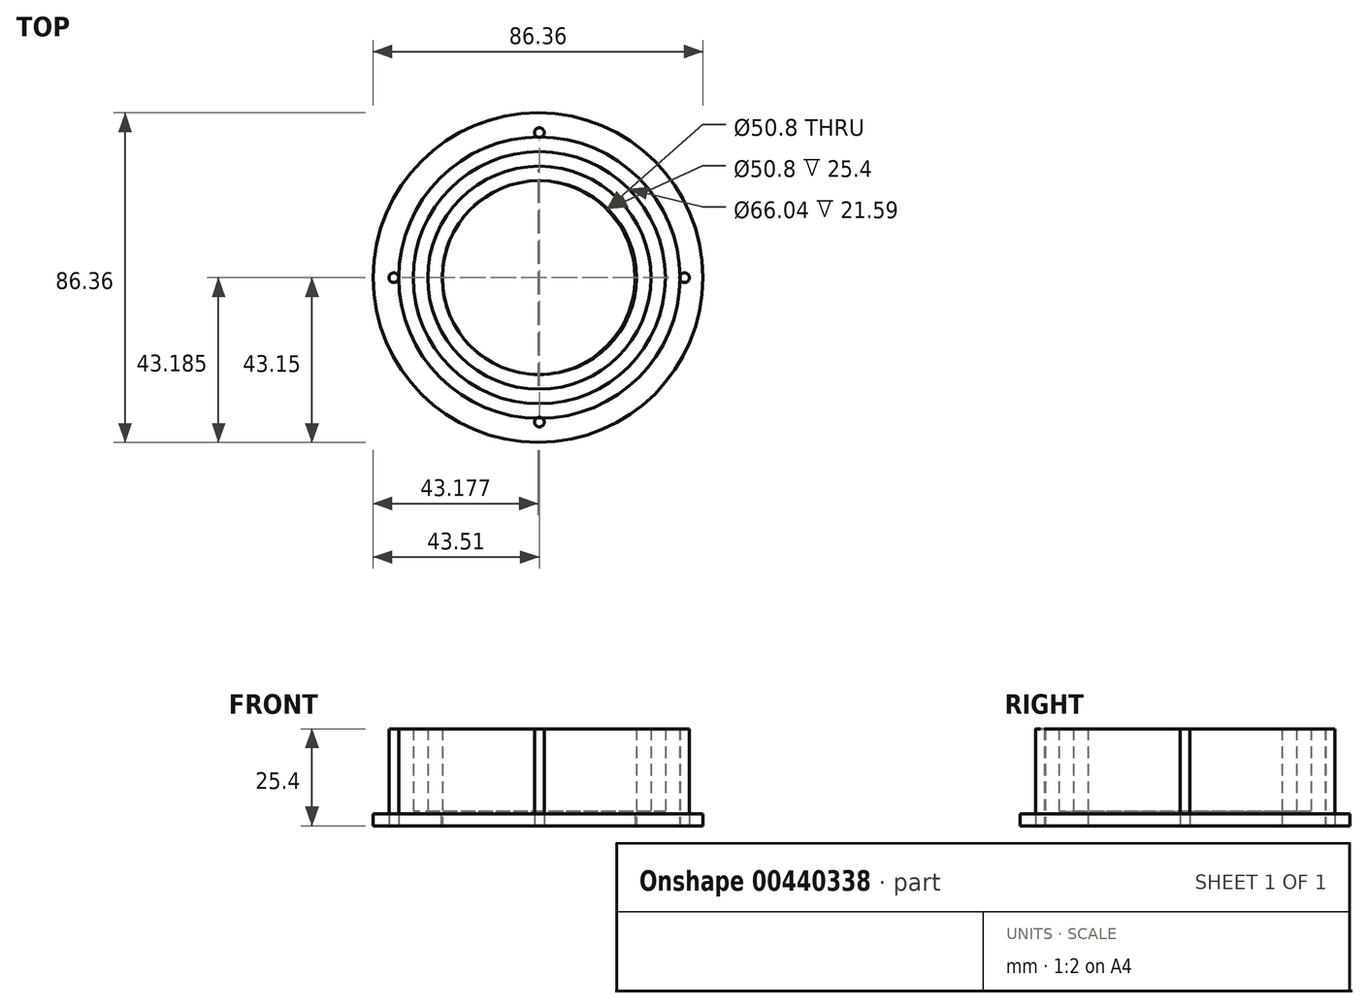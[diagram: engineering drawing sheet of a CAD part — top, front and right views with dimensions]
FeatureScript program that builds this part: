
annotation { "Feature Type Name" : "Feature", "Feature Type Description" : "" }
export const myFeature = defineFeature(function(context is Context, id is Id, definition is map)
    precondition{}
    {
        {
            var Q0;
            Q0=qCreatedBy(makeId("Top.planeOp"),FACE);
            var sketch = newSketch(context, id + "F0", { "sketchPlane" : qUnion([Q0])});
            skCircle(sketch, "E0", {"center": v(0, 0) * mm, "radius": 25.4 * mm});
            skCircle(sketch, "E1.0", {"center": v(0, 0) * mm, "radius": 36.83 * mm});
            skLineSegment(sketch, "E2", {"start": v(0.13, 36.83) * mm, "end": v(0.17, 25.4) * mm});
            skLineSegment(sketch, "E3", {"start": v(-36.83, 0) * mm, "end": v(-25.4, 0) * mm});
            skLineSegment(sketch, "E4", {"start": v(29.07, -22.61) * mm, "end": v(19.97, -15.7) * mm});
            skLineSegment(sketch, "E5", {"start": v(-28.48, -23.35) * mm, "end": v(-19.57, -16.19) * mm});
            skLineSegment(sketch, "E6", {"start": v(-15.63, 33.35) * mm, "end": v(-10.54, 23.1) * mm});
            skLineSegment(sketch, "E7", {"start": v(15.17, 33.56) * mm, "end": v(10.25, 23.24) * mm});
            skLineSegment(sketch, "E8", {"start": v(-34.94, 11.64) * mm, "end": v(-24.14, 7.9) * mm});
            skLineSegment(sketch, "E9", {"start": v(-34.6, -12.63) * mm, "end": v(-23.77, -8.96) * mm});
            skLineSegment(sketch, "E10.0", {"start": v(29.69, -21.8) * mm, "end": v(20.58, -14.88) * mm});
            skLineSegment(sketch, "E11.0", {"start": v(-35.2, 10.92) * mm, "end": v(-24.37, 7.17) * mm});
            skLineSegment(sketch, "E12.0", {"start": v(-36.83, -1.27) * mm, "end": v(-25.37, -1.27) * mm});
            skLineSegment(sketch, "E13.0", {"start": v(-34.84, -11.9) * mm, "end": v(-24.03, -8.24) * mm});
            skLineSegment(sketch, "E14.0", {"start": v(16.09, 33.12) * mm, "end": v(11.17, 22.81) * mm});
            skLineSegment(sketch, "E15.0", {"start": v(-27.84, -24.14) * mm, "end": v(-18.91, -16.96) * mm});
            skLineSegment(sketch, "E16.0", {"start": v(1.14, 36.83) * mm, "end": v(1.19, 25.37) * mm});
            skLineSegment(sketch, "E17.0", {"start": v(-16.77, 32.78) * mm, "end": v(-11.69, 22.55) * mm});
            skLineSegment(sketch, "E18.trimOffspring", {"start": v(-20.47, 15.04) * mm, "end": v(-29.57, 21.95) * mm});
            skLineSegment(sketch, "E19.trimOffspring", {"start": v(-19.85, 15.84) * mm, "end": v(-28.96, 22.76) * mm});
            skLineSegment(sketch, "E20.trimOffspring", {"start": v(20, 15.66) * mm, "end": v(28.9, 22.82) * mm});
            skLineSegment(sketch, "E21.trimOffspring", {"start": v(20.61, 14.84) * mm, "end": v(29.54, 22.03) * mm});
            skLineSegment(sketch, "E22.trimOffspring", {"start": v(24.08, 8.07) * mm, "end": v(34.9, 11.74) * mm});
            skLineSegment(sketch, "E23.trimOffspring", {"start": v(24.31, 7.35) * mm, "end": v(35.14, 11.02) * mm});
            skLineSegment(sketch, "E24.trimOffspring", {"start": v(25.4, 0) * mm, "end": v(36.83, 0) * mm});
            skLineSegment(sketch, "E25.trimOffspring", {"start": v(25.37, -1.27) * mm, "end": v(36.83, -1.27) * mm});
            skLineSegment(sketch, "E26.trimOffspring", {"start": v(23.85, -8.74) * mm, "end": v(34.65, -12.48) * mm});
            skLineSegment(sketch, "E27.trimOffspring", {"start": v(23.58, -9.45) * mm, "end": v(34.4, -13.2) * mm});
            skLineSegment(sketch, "E28.trimOffspring", {"start": v(12.06, -22.36) * mm, "end": v(17.15, -32.6) * mm});
            skLineSegment(sketch, "E29.trimOffspring", {"start": v(10.92, -22.93) * mm, "end": v(16, -33.16) * mm});
            skLineSegment(sketch, "E30.trimOffspring", {"start": v(1.38, -25.36) * mm, "end": v(1.43, -36.82) * mm});
            skLineSegment(sketch, "E31.trimOffspring", {"start": v(0.37, -25.4) * mm, "end": v(0.41, -36.83) * mm});
            skLineSegment(sketch, "E32.trimOffspring", {"start": v(-10.7, -23.03) * mm, "end": v(-15.62, -33.34) * mm});
            skLineSegment(sketch, "E33.trimOffspring", {"start": v(-11.62, -22.59) * mm, "end": v(-16.54, -32.9) * mm});
            skSolve(sketch);
        }
        {
            var Q0;
            Q0=qCreatedBy(makeId("Top.planeOp"),FACE);
            var sketch = newSketch(context, id + "F1", { "sketchPlane" : qUnion([Q0])});
            skCircle(sketch, "E34", {"center": v(0, 38.01) * mm, "radius": 1.27 * mm});
            skCircle(sketch, "E35", {"center": v(0, -37.8) * mm, "radius": 1.27 * mm});
            skCircle(sketch, "E36", {"center": v(38.01, 0) * mm, "radius": 1.27 * mm});
            skCircle(sketch, "E37", {"center": v(-38.12, 0) * mm, "radius": 1.27 * mm});
            skCircle(sketch, "E38.0", {"center": v(0, 0) * mm, "radius": 38.1 * mm});
            skSolve(sketch);
        }
        {
            var Q0;
            Q0=qCreatedBy(makeId("Top.planeOp"),FACE);
            var sketch = newSketch(context, id + "F2", { "sketchPlane" : qUnion([Q0])});
            skCircle(sketch, "E39", {"center": v(-0.33, 0.03) * mm, "radius": 25.4 * mm});
            skCircle(sketch, "E40.0", {"center": v(-0.33, 0.03) * mm, "radius": 43.18 * mm});
            skSolve(sketch);
        }
        {
            var Q0;
            {var subQ0=sQuery(id+"F1.wireOp",EDGE,"E38.0");var subQ1=sQuery(id+"F1.wireOp",EDGE,"E34");var subQ2=makeQuery(id+"F1.imprint","INTERSECT",VERTEX,{"disambiguationData":[OD(0.0)],"derivedFrom":[subQ1,subQ0]});Q0=makeQuery(id+"F1.imprint","IMPRINT",FACE,{"disambiguationData":[TD([[makeQuery(id+"F1.imprint","IMPRINT",EDGE,{"disambiguationData":[TD([[subQ2,-1.0]])],"derivedFrom":subQ1}),1.0]])]});}
            var Q1;
            {var subQ0=sQuery(id+"F1.wireOp",EDGE,"E38.0");var subQ1=sQuery(id+"F1.wireOp",EDGE,"E35");var subQ2=makeQuery(id+"F1.imprint","INTERSECT",VERTEX,{"disambiguationData":[OD(0.0)],"derivedFrom":[subQ1,subQ0]});Q1=makeQuery(id+"F1.imprint","IMPRINT",FACE,{"disambiguationData":[TD([[makeQuery(id+"F1.imprint","IMPRINT",EDGE,{"disambiguationData":[TD([[subQ2,-1.0]])],"derivedFrom":subQ1}),1.0]])]});}
            var Q2;
            {var subQ0=sQuery(id+"F1.wireOp",EDGE,"E38.0");var subQ1=sQuery(id+"F1.wireOp",EDGE,"E36");var subQ2=makeQuery(id+"F1.imprint","INTERSECT",VERTEX,{"disambiguationData":[OD(0.0)],"derivedFrom":[subQ1,subQ0]});Q2=makeQuery(id+"F1.imprint","IMPRINT",FACE,{"disambiguationData":[TD([[makeQuery(id+"F1.imprint","IMPRINT",EDGE,{"disambiguationData":[TD([[subQ2,1.0]])],"derivedFrom":subQ1}),1.0]])]});}
            var Q3;
            {var subQ0=sQuery(id+"F1.wireOp",EDGE,"E38.0");var subQ1=sQuery(id+"F1.wireOp",EDGE,"E37");var subQ2=makeQuery(id+"F1.imprint","INTERSECT",VERTEX,{"disambiguationData":[OD(0.0)],"derivedFrom":[subQ1,subQ0]});Q3=makeQuery(id+"F1.imprint","IMPRINT",FACE,{"disambiguationData":[TD([[makeQuery(id+"F1.imprint","IMPRINT",EDGE,{"disambiguationData":[TD([[subQ2,-1.0]])],"derivedFrom":subQ1}),1.0]])]});}
            var Q4;
            {var subQ0=sQuery(id+"F1.wireOp",EDGE,"E38.0");var subQ1=sQuery(id+"F1.wireOp",EDGE,"E34");var subQ2=makeQuery(id+"F1.imprint","INTERSECT",VERTEX,{"disambiguationData":[OD(0.0)],"derivedFrom":[subQ1,subQ0]});Q4=makeQuery(id+"F1.imprint","IMPRINT",FACE,{"disambiguationData":[TD([[makeQuery(id+"F1.imprint","IMPRINT",EDGE,{"disambiguationData":[TD([[subQ2,1.0]])],"derivedFrom":subQ1}),1.0]])]});}
            var Q5;
            {var subQ0=sQuery(id+"F1.wireOp",EDGE,"E38.0");var subQ1=sQuery(id+"F1.wireOp",EDGE,"E35");var subQ2=makeQuery(id+"F1.imprint","INTERSECT",VERTEX,{"disambiguationData":[OD(0.0)],"derivedFrom":[subQ1,subQ0]});Q5=makeQuery(id+"F1.imprint","IMPRINT",FACE,{"disambiguationData":[TD([[makeQuery(id+"F1.imprint","IMPRINT",EDGE,{"disambiguationData":[TD([[subQ2,1.0]])],"derivedFrom":subQ1}),1.0]])]});}
            var Q6;
            {var subQ0=sQuery(id+"F1.wireOp",EDGE,"E38.0");var subQ1=sQuery(id+"F1.wireOp",EDGE,"E36");var subQ2=makeQuery(id+"F1.imprint","INTERSECT",VERTEX,{"disambiguationData":[OD(0.0)],"derivedFrom":[subQ1,subQ0]});Q6=makeQuery(id+"F1.imprint","IMPRINT",FACE,{"disambiguationData":[TD([[makeQuery(id+"F1.imprint","IMPRINT",EDGE,{"disambiguationData":[TD([[subQ2,-1.0]])],"derivedFrom":subQ1}),1.0]])]});}
            var Q7;
            {var subQ0=sQuery(id+"F1.wireOp",EDGE,"E38.0");var subQ1=sQuery(id+"F1.wireOp",EDGE,"E37");var subQ2=makeQuery(id+"F1.imprint","INTERSECT",VERTEX,{"disambiguationData":[OD(0.0)],"derivedFrom":[subQ1,subQ0]});Q7=makeQuery(id+"F1.imprint","IMPRINT",FACE,{"disambiguationData":[TD([[makeQuery(id+"F1.imprint","IMPRINT",EDGE,{"disambiguationData":[TD([[subQ2,1.0]])],"derivedFrom":subQ1}),1.0]])]});}
            var Q8;
            {var subQ0=sQuery(id+"F0.wireOp",EDGE,"72a65a2f-d1ac-4f3d-be90-c7e949bdd5c3.trimOffspring");Q8=makeQuery(id+"F0.imprint","IMPRINT",FACE,{"disambiguationData":[TD([[makeQuery(id+"F0.imprint","IMPRINT",EDGE,{"derivedFrom":subQ0}),-1.0]])]});}
            var Q9;
            {var subQ0=sQuery(id+"F0.wireOp",EDGE,"RMzSpTs3-MaJD-iskV-XVaw-TTQTuxNfA93L");Q9=makeQuery(id+"F0.imprint","IMPRINT",FACE,{"disambiguationData":[TD([[makeQuery(id+"F0.imprint","IMPRINT",EDGE,{"derivedFrom":subQ0}),1.0]])]});}
            var Q10;
            {var subQ0=sQuery(id+"F0.wireOp",EDGE,"RMzSpTs3-MaJD-iskV-XVaw-TTQTuxNfA93L");Q10=makeQuery(id+"F0.imprint","IMPRINT",FACE,{"disambiguationData":[TD([[makeQuery(id+"F0.imprint","IMPRINT",EDGE,{"derivedFrom":subQ0}),-1.0]])]});}
            var Q11;
            {var subQ0=sQuery(id+"F0.wireOp",EDGE,"s8AOsZZZ-H0nr-ukQr-qXG3-cYkwbSscw6HX");Q11=makeQuery(id+"F0.imprint","IMPRINT",FACE,{"disambiguationData":[TD([[makeQuery(id+"F0.imprint","IMPRINT",EDGE,{"derivedFrom":subQ0}),1.0]])]});}
            var Q12;
            {var subQ0=sQuery(id+"F0.wireOp",EDGE,"s8AOsZZZ-H0nr-ukQr-qXG3-cYkwbSscw6HX");Q12=makeQuery(id+"F0.imprint","IMPRINT",FACE,{"disambiguationData":[TD([[makeQuery(id+"F0.imprint","IMPRINT",EDGE,{"derivedFrom":subQ0}),-1.0]])]});}
            var Q13;
            {var subQ0=sQuery(id+"F0.wireOp",EDGE,"9npQYzSO-Up1v-bGEo-dAbh-Zw8vTuR6PScb");Q13=makeQuery(id+"F0.imprint","IMPRINT",FACE,{"disambiguationData":[TD([[makeQuery(id+"F0.imprint","IMPRINT",EDGE,{"derivedFrom":subQ0}),-1.0]])]});}
            var Q14;
            {var subQ0=sQuery(id+"F0.wireOp",EDGE,"a55828e2-d83b-4d66-912c-f2005ff79f13.trimOffspring");Q14=makeQuery(id+"F0.imprint","IMPRINT",FACE,{"disambiguationData":[TD([[makeQuery(id+"F0.imprint","IMPRINT",EDGE,{"derivedFrom":subQ0}),-1.0]])]});}
            var Q15;
            {var subQ0=sQuery(id+"F0.wireOp",EDGE,"8656dfb7-b0aa-4dbc-9e6f-258041117408.trimOffspring");Q15=makeQuery(id+"F0.imprint","IMPRINT",FACE,{"disambiguationData":[TD([[makeQuery(id+"F0.imprint","IMPRINT",EDGE,{"derivedFrom":subQ0}),-1.0]])]});}
            extrude(context, id + "F3", {"entities" : qUnion([Q0, Q1, Q2, Q3, Q4, Q5, Q6, Q7, Q8, Q9, Q10, Q11, Q12, Q13, Q14, Q15]), "depth" : 25.4 * mm});
        }
        {
            var Q0;
            Q0 = qSketchRegion(id + "F2", true);
            extrude(context, id + "F4", {"entities" : qUnion([Q0]), "depth" : 3.17 * mm});
        }
        {
            var Q0;
            Q0 = qSketchRegion(id + "F0", true);
            extrude(context, id + "F5", {"entities" : qUnion([Q0]), "depth" : 25.4 * mm});
        }
        {
            var Q0;
            Q0=makeQuery(id+"F5.opExtrude","CAP_FACE",FACE,{"disambiguationData":[OSD([sQuery(id+"F0.wireOp",EDGE,"E0"),sQuery(id+"F0.wireOp",EDGE,"E1.0")])],"isStart":false});
            shell(context, id + "F6", {"entities" : qUnion([Q0]), "thickness" : 3.8 * mm});
        }
    });
